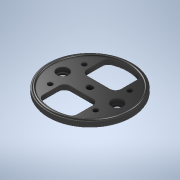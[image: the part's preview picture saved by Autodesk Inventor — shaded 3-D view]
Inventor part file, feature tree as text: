
AUTODESK INVENTOR PART (.ipt)
format: ipt  version: 2020 (Build 240168000, 168)  size: 259,584 bytes
history: native  units: in
note: dims shown in document units (in); Inventor stores cm internally (conversion verified against a paired STEP export)
features: sketch x5, hole x2, extrude x2, fillet x2, revolve x1
ambient origin geometry x8: Origin, YZ Plane, XZ Plane, XY Plane, X Axis, Y Axis, Z Axis, Center Point
bodies: Solid1 (feature_tree)
feature tree (12):
  revolve  "Revolution1"  [1 undecoded]
  hole  "Hole2"  [1 undecoded]
  extrude  "Extrusion2"  Depth=2.4in
  extrude  "Extrusion3"  Depth=0.25in
  fillet  "Fillet1"  Radius=0.216in
  fillet  "Fillet2"  [1 undecoded]
  hole  "Hole3"  [1 undecoded]
  sketch  "Sketch1"  dims[d0=1.85in d1=0.25in]
  sketch  "Sketch4"  dims[d2=1.75in d3=0.11in]
  sketch  "Sketch5"  dims[d4=90.0deg d24=2.4in]
  sketch  "Sketch6"  dims[d25=0.35in d26=0.75in d27=0.51in d28=0.188in d29=0.5635in d30=1.0in d31=0.8108in d32=0.25in d33=0.216in d34=0.0in d35=0.0in]
  sketch  "Sketch8"  dims[d36=3.3in d37=1.5in d38=0.75in d39=1.0in d40=0.0in d41=0.25in d43=0.0625in d44=0.01in d53=2.0in d54=1.5in d55=0.205in d56=0.75in d57=0.411in d58=0.25in d59=0.5635in d60=1.0in d61=0.0in]
note: 4 required parameter values undecoded (feature->parameter linkage not recoverable at this tier; creation-order binding heuristic only, values carry confidence <= 0.55)